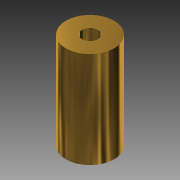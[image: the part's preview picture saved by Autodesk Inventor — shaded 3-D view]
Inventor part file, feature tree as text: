
AUTODESK INVENTOR PART (.ipt)
format: ipt  version: 2015 (Build 190159000, 159)  size: 102,912 bytes
history: native  units: mm
features: extrude x2, sketch x2, other x1
ambient origin geometry x8: Origin, YZ Plane, XZ Plane, XY Plane, X Axis, Y Axis, Z Axis, Center Point
bodies: Body1 (feature_tree)
feature tree (5):
  other  "ソリッド1"
  extrude  "押し出し1"  Depth=9.0mm
  extrude  "押し出し2"  Depth=18.0mm TaperAngle=0.0deg
  sketch  "スケッチ1"
  sketch  "スケッチ2"
